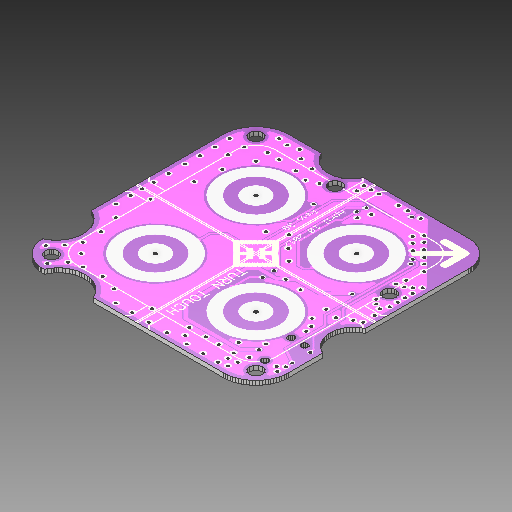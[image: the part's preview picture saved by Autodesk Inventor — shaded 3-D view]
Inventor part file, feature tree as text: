
AUTODESK INVENTOR PART (.ipt)
format: ipt  version: 2018 (Build 220112000, 112)  size: 3,526,144 bytes
history: native  units: in
note: dims shown in document units (in); Inventor stores cm internally (conversion verified against a paired STEP export)
features: other x5, sketch x2, extrude x1, move_body x1
ambient origin geometry x8: Origin, YZ Plane, XZ Plane, XY Plane, X Axis, Y Axis, Z Axis, Center Point
bodies: Solid1 (feature_tree)
feature tree (9):
  extrude  "Extrusion1"  Depth=0.026in TaperAngle=0.0deg
  move_body  "Move Body1"
  other  "Decal1"
  other  "Decal2"
  other  "PCB"
  sketch  "Sketch3"  dims[d0=1.453in d1=0.026in d2=0.0in]
  other  "Image1"
  sketch  "Sketch4"  dims[d3=90.0deg d4=90.0deg]
  other  "Image2"
